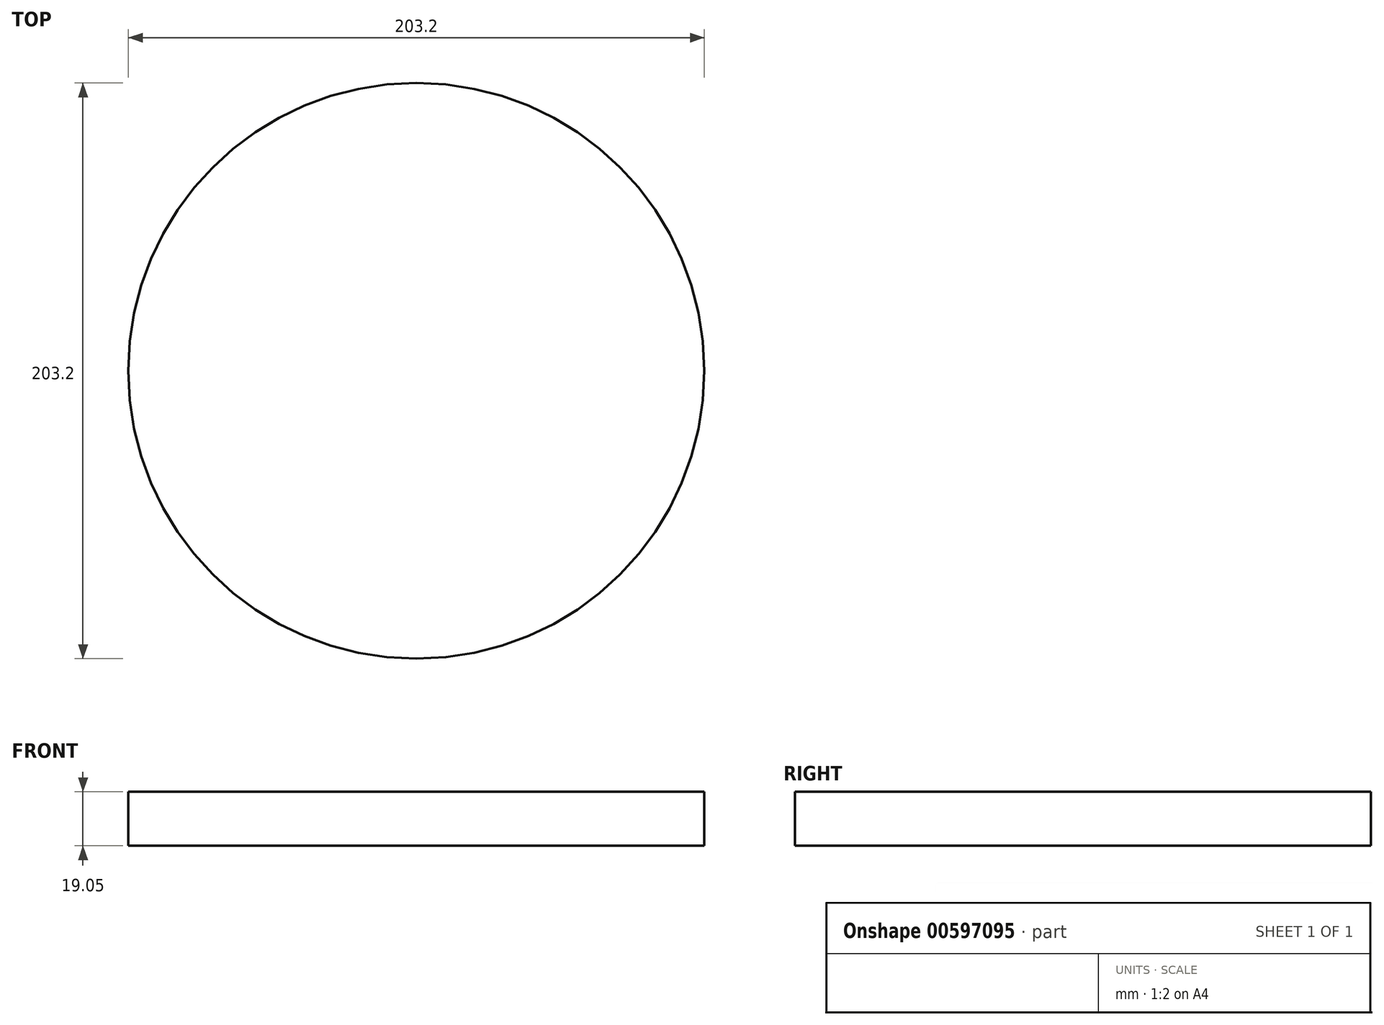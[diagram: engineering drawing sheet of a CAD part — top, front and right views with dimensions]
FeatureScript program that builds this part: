
annotation { "Feature Type Name" : "Feature", "Feature Type Description" : "" }
export const myFeature = defineFeature(function(context is Context, id is Id, definition is map)
    precondition{}
    {
        {
            var Q0;
            Q0=qCreatedBy(makeId("Top.planeOp"),FACE);
            var sketch = newSketch(context, id + "F0", { "sketchPlane" : qUnion([Q0])});
            skCircle(sketch, "E0", {"center": v(0, 0) * mm, "radius": 101.6 * mm});
            skSolve(sketch);
        }
        {
            var Q0;
            Q0 = qSketchRegion(id + "F0", true);
            extrude(context, id + "F1", {"entities" : qUnion([Q0]), "depth" : 19.05 * mm, "offsetDistance" : 25.4 * mm});
        }
    });
